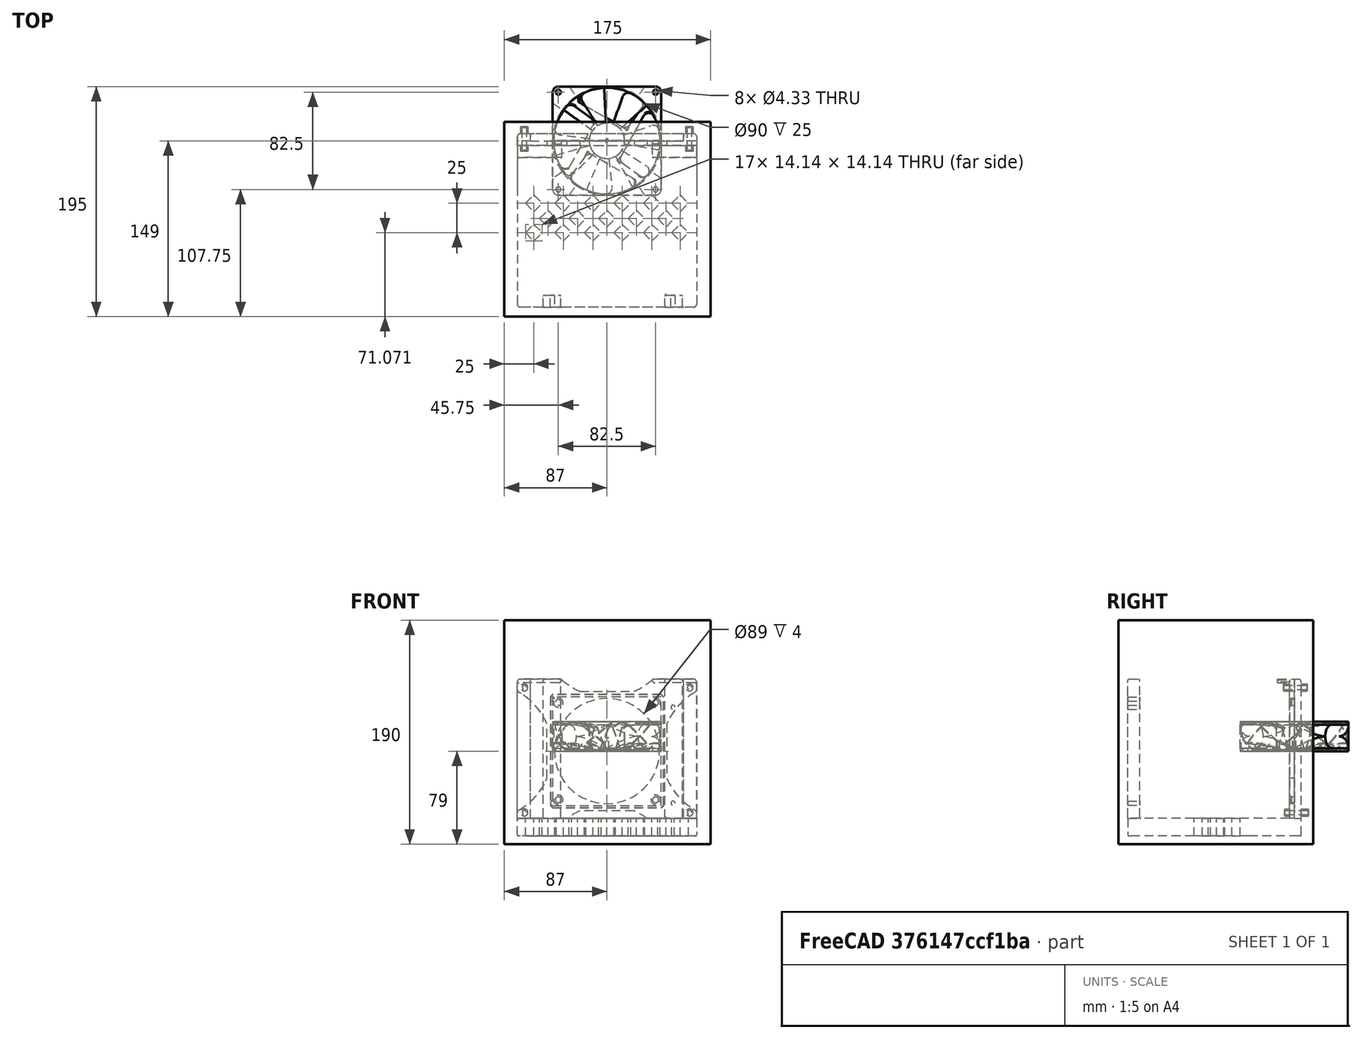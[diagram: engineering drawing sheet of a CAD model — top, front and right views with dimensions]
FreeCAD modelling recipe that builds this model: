
FCSTD DOCUMENT  (FreeCAD 0.21R33668 +7 (Git))
Label: Odroid_h4_mount_July_11_2024
License: All rights reserved
LicenseURL: https://en.wikipedia.org/wiki/All_rights_reserved
objects: Part::Box×24, Part::Cylinder×12, Part::MultiFuse×11, Part::Feature×3, Part::Cut×3, App::Part×2, Part::Fillet×2, Mesh::Feature×1
note: 55 computed .brp shape members not serialized (recipe doc carries the construction recipe); baked Part::Feature solids carry a one-line shape summary decoded from their .brp

FEATURE [Part::Feature] Part__Feature  label="fan form"
  shape: bbox 105.3 x 105.3 x 25.46 mm, 118 faces (baked)
FEATURE [Part::Feature] Part__Feature001  label="fan"
  Placement = pos=(0,0,1.25) rot=(0,0,-1;0.171016rad)
  shape: bbox 91.23 x 90.98 x 28.5 mm, 54 faces (baked)
FEATURE [App::Part] Assem1  label="Fan"
  Group = -> [Part__Feature,Part__Feature001]
  Origin = -> Origin
  Placement = pos=(0,-5.5,0) rot=(1,0,0;1.5708rad)
FEATURE [Part::Box] Box  label="Base_Plate"
  AttacherType = Attacher::AttachEngine3D
  Height = 45
  Length = 152
  Placement = pos=(76,6,-57) rot=(0,0.707107,-0.707107;3.14159rad)
  Width = 15
FEATURE [Part::Box] Box001  label="Cube001"
  AttacherType = Attacher::AttachEngine3D
  Height = 118
  Length = 11
  Placement = pos=(65,0,-57) rot=(0,0,1;0rad)
  Width = 6
FEATURE [Part::Box] Box002  label="Cube002"
  AttacherType = Attacher::AttachEngine3D
  Height = 118
  Length = 11
  Placement = pos=(-76,0,-57) rot=(0,0,1;0rad)
  Width = 6
FEATURE [Part::Feature] Part__Feature002  label="Fan_mount"
  Placement = pos=(0,0,0) rot=(-1,0,0;1.5708rad)
  shape: bbox 152 x 14.25 x 122 mm, 73 faces (baked)
FEATURE [Part::MultiFuse] Fusion  label="Base"
  Shapes = -> [Box,Box001,Box002]
FEATURE [Part::Fillet] Fillet  label="Fan_hold"
  Base = -> Fusion
  Edges = 2 edges r=2.5: [Edge7,Edge36]
FEATURE [Part::Box] Box003  label="Volume "
  AttacherType = Attacher::AttachEngine3D
  Height = 165
  Length = 175
  Placement = pos=(88,16,111) rot=(0,0.707107,-0.707107;3.14159rad)
  Width = 190
FEATURE [Mesh::Feature] Odroid_H004  label="Odroid-H004"
  Placement = pos=(-50,-110,62) rot=(1,0,0;4.71239rad)
FEATURE [Part::Box] Box004  label="Base_Plate001"
  AttacherType = Attacher::AttachEngine3D
  Height = 102
  Length = 152
  Placement = pos=(76,-39,-57) rot=(0,0.707107,-0.707107;3.14159rad)
  Width = 15
FEATURE [Part::Box] Box006  label="Cube003"
  AttacherType = Attacher::AttachEngine3D
  Height = 20
  Length = 10
  Placement = pos=(-35,-60,0) rot=(0,0,1;0.785398rad)
  Width = 10
FEATURE [Part::Box] Box007  label="Cube004"
  AttacherType = Attacher::AttachEngine3D
  Height = 20
  Length = 10
  Placement = pos=(-10,-60,0) rot=(0,0,1;0.785398rad)
  Width = 10
FEATURE [Part::Box] Box008  label="Cube005"
  AttacherType = Attacher::AttachEngine3D
  Height = 20
  Length = 10
  Placement = pos=(15,-60,0) rot=(0,0,1;0.785398rad)
  Width = 10
FEATURE [Part::Box] Box009  label="Cube006"
  AttacherType = Attacher::AttachEngine3D
  Height = 20
  Length = 10
  Placement = pos=(40,-60,0) rot=(0,0,1;0.785398rad)
  Width = 10
FEATURE [Part::Box] Box010  label="Cube007"
  AttacherType = Attacher::AttachEngine3D
  Height = 20
  Length = 10
  Placement = pos=(64,-60,0) rot=(0,0,1;0.785398rad)
  Width = 10
FEATURE [Part::Box] Box011  label="Cube008"
  AttacherType = Attacher::AttachEngine3D
  Height = 20
  Length = 10
  Placement = pos=(-60,-60,0) rot=(0,0,1;0.785398rad)
  Width = 10
FEATURE [Part::Box] Box012  label="Cube009"
  AttacherType = Attacher::AttachEngine3D
  Height = 20
  Length = 10
  Placement = pos=(-35,-60,0) rot=(0,0,1;0.785398rad)
  Width = 10
FEATURE [Part::Box] Box013  label="Cube010"
  AttacherType = Attacher::AttachEngine3D
  Height = 20
  Length = 10
  Placement = pos=(-10,-60,0) rot=(0,0,1;0.785398rad)
  Width = 10
FEATURE [Part::Box] Box014  label="Cube011"
  AttacherType = Attacher::AttachEngine3D
  Height = 20
  Length = 10
  Placement = pos=(15,-60,0) rot=(0,0,1;0.785398rad)
  Width = 10
FEATURE [Part::Box] Box015  label="Cube012"
  AttacherType = Attacher::AttachEngine3D
  Height = 20
  Length = 10
  Placement = pos=(40,-60,0) rot=(0,0,1;0.785398rad)
  Width = 10
FEATURE [Part::MultiFuse] Fusion002  label="CubeLine002"
  Placement = pos=(10,-13,0) rot=(0,0,1;0rad)
  Shapes = -> [Box011,Box012,Box013,Box014,Box015]
FEATURE [Part::Box] Box016  label="Cube013"
  AttacherType = Attacher::AttachEngine3D
  Height = 20
  Length = 10
  Placement = pos=(-60,-60,0) rot=(0,0,1;0.785398rad)
  Width = 10
FEATURE [Part::Box] Box017  label="Cube014"
  AttacherType = Attacher::AttachEngine3D
  Height = 20
  Length = 10
  Placement = pos=(-35,-60,0) rot=(0,0,1;0.785398rad)
  Width = 10
FEATURE [Part::Box] Box018  label="Cube015"
  AttacherType = Attacher::AttachEngine3D
  Height = 20
  Length = 10
  Placement = pos=(-10,-60,0) rot=(0,0,1;0.785398rad)
  Width = 10
FEATURE [Part::Box] Box019  label="Cube016"
  AttacherType = Attacher::AttachEngine3D
  Height = 20
  Length = 10
  Placement = pos=(15,-60,0) rot=(0,0,1;0.785398rad)
  Width = 10
FEATURE [Part::Box] Box020  label="Cube017"
  AttacherType = Attacher::AttachEngine3D
  Height = 20
  Length = 10
  Placement = pos=(40,-60,0) rot=(0,0,1;0.785398rad)
  Width = 10
FEATURE [Part::Box] Box021  label="Cube018"
  AttacherType = Attacher::AttachEngine3D
  Height = 20
  Length = 10
  Placement = pos=(64,-60,0) rot=(0,0,1;0.785398rad)
  Width = 10
FEATURE [Part::MultiFuse] Fusion003  label="CubeLine003"
  Placement = pos=(-2,-25,0) rot=(0,0,1;0rad)
  Shapes = -> [Box016,Box017,Box018,Box019,Box020,Box021]
FEATURE [Part::Box] Box005  label="Cube"
  AttacherType = Attacher::AttachEngine3D
  Height = 20
  Length = 10
  Placement = pos=(-60,-60,0) rot=(0,0,1;0.785398rad)
  Width = 10
FEATURE [Part::MultiFuse] Fusion001  label="CubeLine1"
  Placement = pos=(-2,0,0) rot=(0,0,1;0rad)
  Shapes = -> [Box005,Box006,Box007,Box008,Box009,Box010]
FEATURE [Part::MultiFuse] Fusion004
  Placement = pos=(0,0,-75) rot=(0,0,1;0rad)
  Shapes = -> [Fusion001,Fusion002,Fusion003]
FEATURE [Part::Cut] Cut  label="BasePlate01"
  Base = -> Box004
  Tool = -> Fusion004
FEATURE [Part::Box] Box022  label="Cube019"
  AttacherType = Attacher::AttachEngine3D
  Height = 118
  Length = 15
  Placement = pos=(49,-141,-57) rot=(0,0,1;0rad)
  Width = 10
FEATURE [Part::Box] Box023  label="Cube020"
  AttacherType = Attacher::AttachEngine3D
  Height = 118
  Length = 15
  Placement = pos=(-54,-141,-57) rot=(0,0,1;0rad)
  Width = 10
FEATURE [Part::MultiFuse] Fusion005  label="Base_H4"
  Shapes = -> [Cut,Box022,Box023]
FEATURE [Part::Cylinder] Cylinder
  Angle = 360
  AttacherType = Attacher::AttachEngine3D
  FirstAngle = 0
  Height = 20
  Placement = pos=(-46.19,-136,44.22) rot=(1,0,0;1.5708rad)
  Radius = 1.75
  SecondAngle = 0
FEATURE [Part::Cylinder] Cylinder001
  Angle = 360
  AttacherType = Attacher::AttachEngine3D
  FirstAngle = 0
  Height = 20
  Placement = pos=(-46.19,-136,-44.19) rot=(1,0,0;1.5708rad)
  Radius = 1.75
  SecondAngle = 0
FEATURE [Part::Cylinder] Cylinder002
  Angle = 360
  AttacherType = Attacher::AttachEngine3D
  FirstAngle = 0
  Height = 20
  Placement = pos=(56.05,-136,-44.2) rot=(1,0,0;1.5708rad)
  Radius = 1.75
  SecondAngle = 0
FEATURE [Part::Cylinder] Cylinder003
  Angle = 360
  AttacherType = Attacher::AttachEngine3D
  FirstAngle = 0
  Height = 20
  Placement = pos=(56.05,-136,37.23) rot=(1,0,0;1.5708rad)
  Radius = 1.75
  SecondAngle = 0
FEATURE [Part::MultiFuse] Fusion006  label="Mount_cut"
  Placement = pos=(0,10,0) rot=(0,0,1;0rad)
  Shapes = -> [Cylinder,Cylinder001,Cylinder002,Cylinder003]
FEATURE [Part::Cut] Cut001  label="h4_mount"
  Base = -> Fusion005
  Tool = -> Fusion006
FEATURE [Part::MultiFuse] Fusion007  label="Mount01"
  Shapes = -> [Cut001,Fillet,Part__Feature002]
FEATURE [Part::Fillet] Fillet001  label="Mount"
  Base = -> Fusion007
  Edges = 29 edges: [Edge165 r=2.5,Edge169 r=2.5,Edge171 r=2.5,Edge172 r=1,Edge178 r=1,Edge182 r=1,Edge183 r=1,Edge184 r=1,Edge187 r=1,Edge188 r=1,Edge264 r=1,Edge269 r=2.5,Edge300 r=2.5,Edge301 r=1,Edge302 r=2.5,Edge303 r=1,Edge307 r=1,Edge308 r=1,Edge309 r=1,Edge310 r=1,Edge314 r=1,Edge316 r=1,Edge317 r=1,Edge318 r=1,Edge319 r=1,Edge323 r=1,Edge324 r=1,Edge461 r=1,Edge464 r=1]
FEATURE [Part::Cylinder] Cylinder004
  Angle = 360
  AttacherType = Attacher::AttachEngine3D
  FirstAngle = 0
  Height = 30
  Placement = pos=(70,17,54) rot=(1,0,0;1.5708rad)
  Radius = 1.75
  SecondAngle = 0
FEATURE [Part::Cylinder] Cylinder005
  Angle = 360
  AttacherType = Attacher::AttachEngine3D
  FirstAngle = 0
  Height = 30
  Placement = pos=(-70,17,54) rot=(1,0,0;1.5708rad)
  Radius = 1.75
  SecondAngle = 0
FEATURE [Part::Cylinder] Cylinder006
  Angle = 360
  AttacherType = Attacher::AttachEngine3D
  FirstAngle = 0
  Height = 30
  Placement = pos=(70,18,-52) rot=(1,0,0;1.5708rad)
  Radius = 1.75
  SecondAngle = 0
FEATURE [Part::Cylinder] Cylinder007
  Angle = 360
  AttacherType = Attacher::AttachEngine3D
  FirstAngle = 0
  Height = 30
  Placement = pos=(-70,18,-52) rot=(1,0,0;1.5708rad)
  Radius = 1.75
  SecondAngle = 0
FEATURE [Part::MultiFuse] Fusion008  label="m3_mount_Cut"
  Shapes = -> [Cylinder004,Cylinder005,Cylinder006,Cylinder007]
FEATURE [Part::Cylinder] Cylinder008
  Angle = 360
  AttacherType = Attacher::AttachEngine3D
  FirstAngle = 0
  Height = 20
  Placement = pos=(70,17,54) rot=(1,0,0;1.5708rad)
  Radius = 3
  SecondAngle = 0
FEATURE [Part::Cylinder] Cylinder009
  Angle = 360
  AttacherType = Attacher::AttachEngine3D
  FirstAngle = 0
  Height = 20
  Placement = pos=(-70,17,54) rot=(1,0,0;1.5708rad)
  Radius = 3
  SecondAngle = 0
FEATURE [Part::Cylinder] Cylinder010
  Angle = 360
  AttacherType = Attacher::AttachEngine3D
  FirstAngle = 0
  Height = 20
  Placement = pos=(70,18,-52) rot=(1,0,0;1.5708rad)
  Radius = 3
  SecondAngle = 0
FEATURE [Part::Cylinder] Cylinder011
  Angle = 360
  AttacherType = Attacher::AttachEngine3D
  FirstAngle = 0
  Height = 20
  Placement = pos=(-70,18,-52) rot=(1,0,0;1.5708rad)
  Radius = 3
  SecondAngle = 0
FEATURE [Part::MultiFuse] Fusion009  label="m3_mount_support"
  Placement = pos=(0,-6,0) rot=(0,0,1;0rad)
  Shapes = -> [Cylinder008,Cylinder009,Cylinder010,Cylinder011]
FEATURE [Part::MultiFuse] Fusion010  label="Mount002"
  Shapes = -> [Fillet001,Fusion009]
FEATURE [Part::Cut] Cut002  label="Base001"
  Base = -> Fusion010
  Tool = -> Fusion008
FEATURE [App::Part] Part  label="H4_Mount"
  Group = -> [Assem1,Box003,Odroid_H004,Fillet001,Fillet,Cut,Fusion006,Fusion007,Cut001,Fusion002,Fusion,Fusion003,Fusion001,Fusion004,Fusion005,Box004,Box,Box001,Box002,Part__Feature002,Box006,Box007,Box008,Box009,Box010,Box011,Box012,Box013,Box014,Box015,Box016,Box023,Cylinder,Cylinder001,Cylinder002,Cylinder003,Fusion008,Fusion009,Fusion010,Cylinder004,Cylinder011,Cylinder008,Cylinder010,Cylinder007,+11 more]
  Origin = -> Origin001
